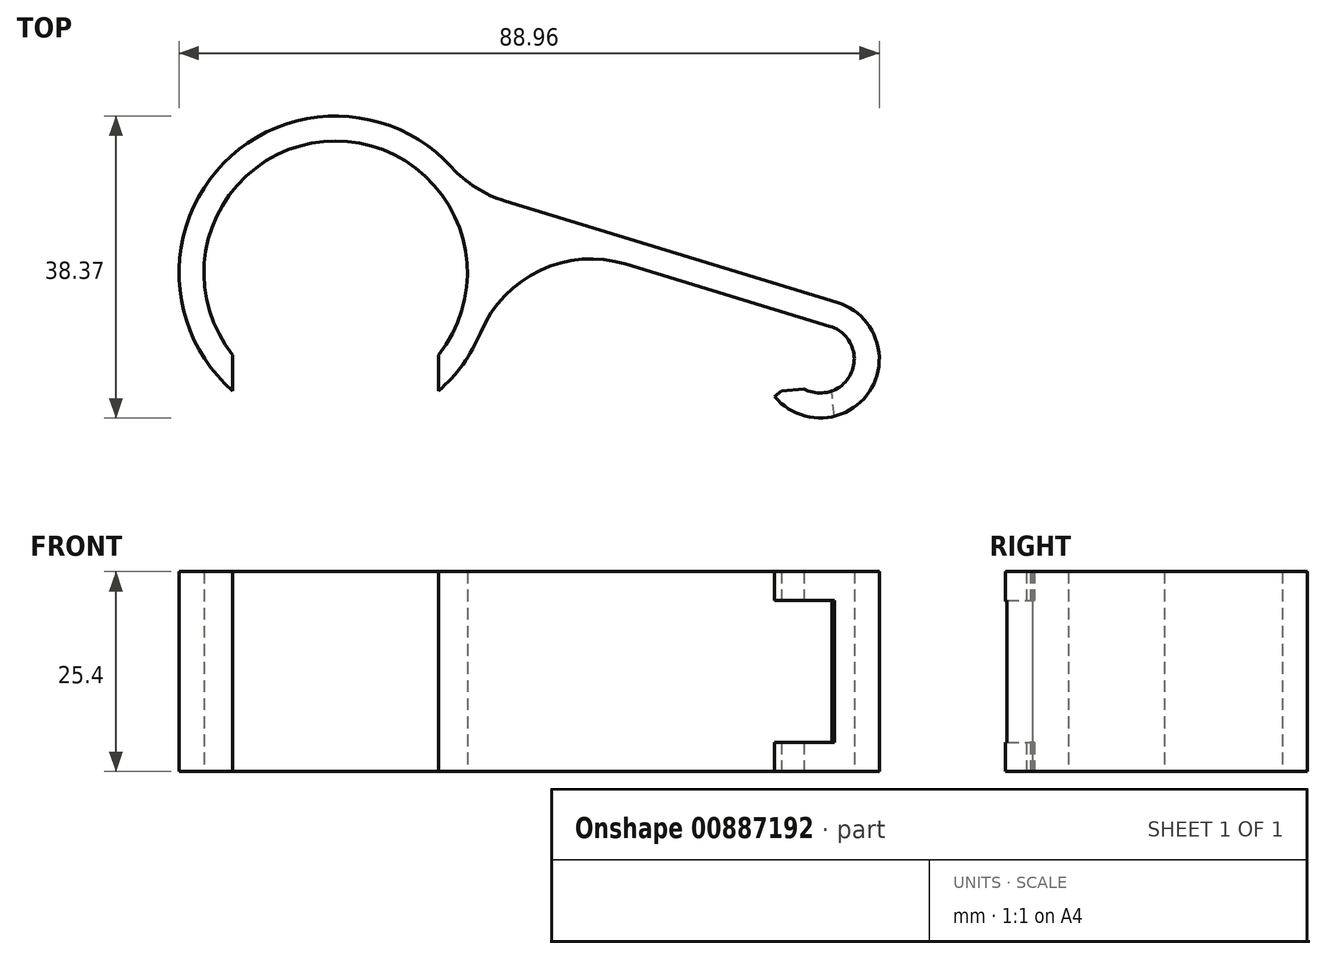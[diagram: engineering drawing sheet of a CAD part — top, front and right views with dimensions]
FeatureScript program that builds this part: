
annotation { "Feature Type Name" : "Feature", "Feature Type Description" : "" }
export const myFeature = defineFeature(function(context is Context, id is Id, definition is map)
    precondition{}
    {
        {
            var Q0;
            Q0=qCreatedBy(makeId("Top.planeOp"),FACE);
            var sketch = newSketch(context, id + "F0", { "sketchPlane" : qUnion([Q0])});
            skArc(sketch, "E0", {"start": v(13.08, -10.44) * mm, "mid": v(0, 16.73) * mm, "end": v(-13.08, -10.44) * mm});
            skLineSegment(sketch, "E1", {"start": v(13.08, -10.44) * mm, "end": v(13.08, -15.01) * mm});
            skArc(sketch, "E2.0", {"start": v(13.08, -15.01) * mm, "mid": v(19.25, -5.07) * mm, "end": v(18.77, 6.63) * mm});
            skLineSegment(sketch, "E3.MirrorCS", {"start": v(-13.08, -10.44) * mm, "end": v(-13.08, -15.01) * mm});
            skLineSegment(sketch, "E4", {"start": v(16.9, 10.52) * mm, "end": v(63.73, -3.77) * mm});
            skLineSegment(sketch, "E5.0", {"start": v(18.77, 6.63) * mm, "end": v(62.8, -6.8) * mm});
            skArc(sketch, "E6.trimOffspring", {"start": v(16.9, 10.52) * mm, "mid": v(-12.9, 15.16) * mm, "end": v(-13.08, -15.01) * mm});
            skArc(sketch, "E7", {"start": v(62.8, -6.8) * mm, "mid": v(65.15, -13.35) * mm, "end": v(58.2, -13.71) * mm});
            skArc(sketch, "E8.0", {"start": v(63.73, -3.77) * mm, "mid": v(67.8, -15.1) * mm, "end": v(55.77, -15.74) * mm});
            skLineSegment(sketch, "E9", {"start": v(58.2, -13.71) * mm, "end": v(55.77, -15.74) * mm});
            skSolve(sketch);
        }
        {
            var Q0;
            Q0 = qSketchRegion(id + "F0", true);
            extrude(context, id + "F1", {"entities" : qUnion([Q0]), "depth" : 25.4 * mm, "offsetDistance" : 25.4 * mm});
        }
        {
            var Q0;
            Q0=makeQuery(id+"F1.opExtrude","SWEPT_EDGE",EDGE,{"disambiguationData":[OSD([sQuery(id+"F0.wireOp",EDGE,"E4"),sQuery(id+"F0.wireOp",EDGE,"E6.trimOffspring")])]});
            var Q1;
            Q1=makeQuery(id+"F1.opExtrude","SWEPT_EDGE",EDGE,{"disambiguationData":[OSD([sQuery(id+"F0.wireOp",EDGE,"E2.0"),sQuery(id+"F0.wireOp",EDGE,"E5.0")])]});
            fillet(context, id + "F2", {"entities" : qUnion([Q0, Q1]), "radius" : 15.24 * mm, "tangentPropagation" : true, "allowEdgeOverflow" : false});
        }
        {
            var Q0;
            Q0=makeQuery(id+"F1.opExtrude","SWEPT_EDGE",EDGE,{"disambiguationData":[OSD([sQuery(id+"F0.wireOp",EDGE,"E7"),sQuery(id+"F0.wireOp",EDGE,"E9")])]});
            chamfer(context, id + "F3", {"entities" : qUnion([Q0]), "width" : 2.54 * mm, "tangentPropagation" : true});
        }
        {
            var Q0;
            Q0=makeQuery(id+"F3.opChamfer","BLEND_FACE",FACE,{"disambiguationData":[OSD([sQuery(id+"F0.wireOp",EDGE,"E7"),sQuery(id+"F0.wireOp",EDGE,"E9")])]});
            var sketch = newSketch(context, id + "F4", { "sketchPlane" : qUnion([Q0])});
            skLineSegment(sketch, "E10", {"start": v(-61.3, 12.7) * mm, "end": v(-61.3, 21.71) * mm});
            skLineSegment(sketch, "E11", {"start": v(-61.3, 21.71) * mm, "end": v(-50.68, 21.71) * mm});
            skLineSegment(sketch, "E12", {"start": v(-50.68, 21.71) * mm, "end": v(-50.68, 12.7) * mm});
            skLineSegment(sketch, "E13", {"start": v(-61.3, 12.7) * mm, "end": v(-50.68, 12.7) * mm});
            skPoint(sketch, "E14.orphan", {"position": v(-50.68, 14.97) * mm});
            skLineSegment(sketch, "E15.MirrorCS", {"start": v(-61.3, 12.7) * mm, "end": v(-61.3, 3.69) * mm});
            skLineSegment(sketch, "E16.MirrorCS", {"start": v(-61.3, 3.69) * mm, "end": v(-50.68, 3.69) * mm});
            skLineSegment(sketch, "E17.MirrorCS", {"start": v(-50.68, 3.69) * mm, "end": v(-50.68, 12.7) * mm});
            skPoint(sketch, "E18.MirrorP", {"position": v(-50.68, 10.43) * mm});
            skSolve(sketch);
        }
        {
            var Q0;
            {var subQ0=sQuery(id+"F4.wireOp",EDGE,"E15.MirrorCS");Q0=makeQuery(id+"F4.imprint","IMPRINT",FACE,{"disambiguationData":[TD([[makeQuery(id+"F4.imprint","IMPRINT",EDGE,{"derivedFrom":subQ0}),1.0]])]});}
            var Q1;
            {var subQ0=sQuery(id+"F4.wireOp",EDGE,"E10");Q1=makeQuery(id+"F4.imprint","IMPRINT",FACE,{"disambiguationData":[TD([[makeQuery(id+"F4.imprint","IMPRINT",EDGE,{"derivedFrom":subQ0}),-1.0]])]});}
            var Q2;
            {var subQ0=sQuery(id+"F4.wireOp",EDGE,"E11");var subQ1=sQuery(id+"F0.wireOp",EDGE,"E7");var subQ2=sQuery(id+"F0.wireOp",EDGE,"E9");var subQ3=makeQuery(id+"F1.opExtrude","SWEPT_EDGE",EDGE,{"disambiguationData":[OSD([subQ1,subQ2])]});var subQ4=makeQuery(id+"F3.opChamfer","BLEND_EDGE",EDGE,{"blendedFrom":[subQ3,makeQuery(id+"F1.opExtrude","SWEPT_FACE",FACE,{"disambiguationData":[OSD([subQ1])]})],"blendedInto":[makeQuery(id+"F1.opExtrude","SWEPT_FACE",FACE,{"disambiguationData":[OSD([subQ1])]})]});var subQ5=makeQuery(id+"F4.imprint","INTERSECT",VERTEX,{"derivedFrom":[subQ4,subQ0]});Q2=makeQuery(id+"F4.imprint","IMPRINT",FACE,{"disambiguationData":[TD([[makeQuery(id+"F4.imprint","IMPRINT",EDGE,{"disambiguationData":[TD([[subQ5,-1.0]])],"derivedFrom":subQ0}),-1.0]])]});}
            var Q3;
            {var subQ0=sQuery(id+"F4.wireOp",EDGE,"E13");var subQ1=sQuery(id+"F0.wireOp",EDGE,"E7");var subQ2=sQuery(id+"F0.wireOp",EDGE,"E9");var subQ3=makeQuery(id+"F1.opExtrude","SWEPT_EDGE",EDGE,{"disambiguationData":[OSD([subQ1,subQ2])]});var subQ4=makeQuery(id+"F3.opChamfer","BLEND_EDGE",EDGE,{"blendedFrom":[subQ3,makeQuery(id+"F1.opExtrude","SWEPT_FACE",FACE,{"disambiguationData":[OSD([subQ1])]})],"blendedInto":[makeQuery(id+"F1.opExtrude","SWEPT_FACE",FACE,{"disambiguationData":[OSD([subQ1])]})]});var subQ5=makeQuery(id+"F4.imprint","INTERSECT",VERTEX,{"derivedFrom":[subQ4,subQ0]});Q3=makeQuery(id+"F4.imprint","IMPRINT",FACE,{"disambiguationData":[TD([[makeQuery(id+"F4.imprint","IMPRINT",EDGE,{"disambiguationData":[TD([[subQ5,-1.0]])],"derivedFrom":subQ0}),-1.0]])]});}
            var Q4;
            {var subQ0=sQuery(id+"F4.wireOp",EDGE,"E17.MirrorCS");Q4=makeQuery(id+"F4.imprint","IMPRINT",FACE,{"disambiguationData":[TD([[makeQuery(id+"F4.imprint","IMPRINT",EDGE,{"derivedFrom":subQ0}),1.0]])]});}
            var Q5;
            {var subQ0=sQuery(id+"F4.wireOp",EDGE,"E12");Q5=makeQuery(id+"F4.imprint","IMPRINT",FACE,{"disambiguationData":[TD([[makeQuery(id+"F4.imprint","IMPRINT",EDGE,{"derivedFrom":subQ0}),-1.0]])]});}
            extrude(context, id + "F5", {"entities" : qUnion([Q0, Q1, Q2, Q3, Q4, Q5]), "operationType" : NewBodyOperationType.REMOVE, "oppositeDirection" : true, "depth" : 25.4 * mm, "offsetDistance" : 25.4 * mm});
        }
    });
